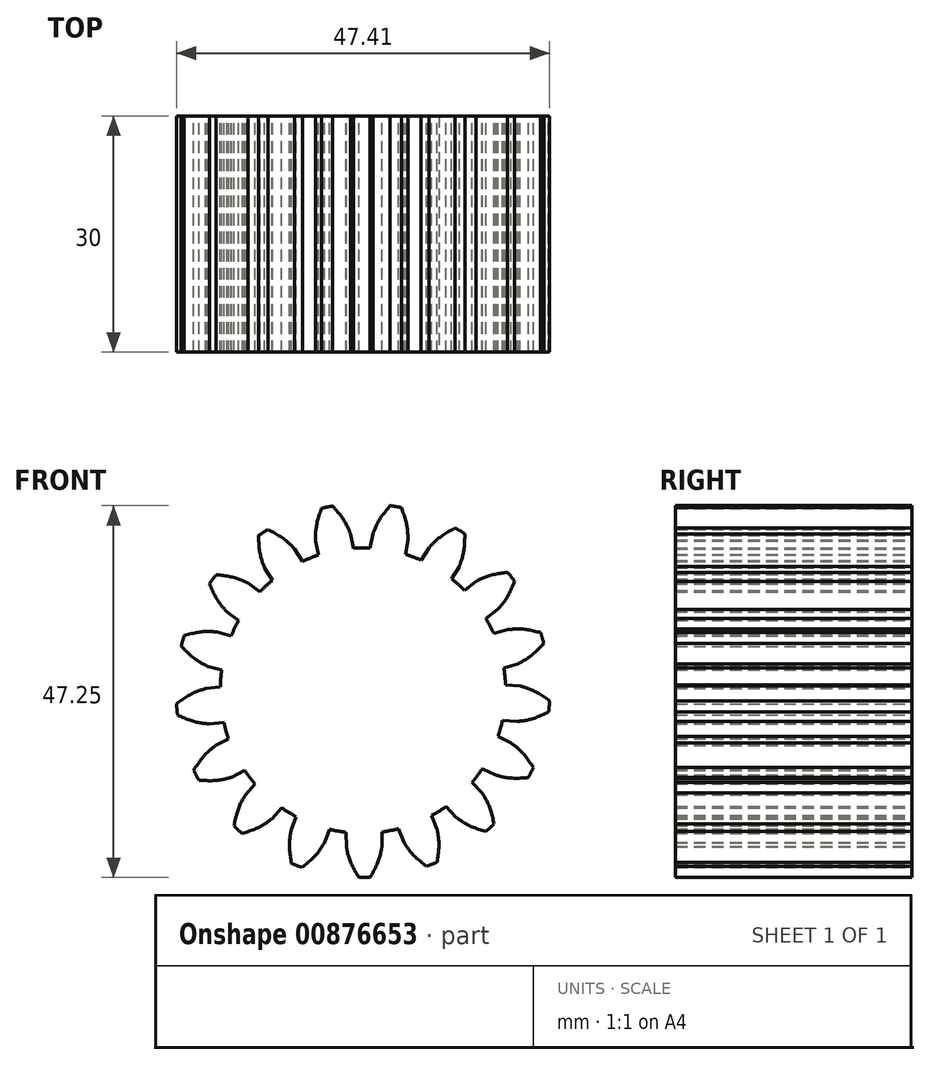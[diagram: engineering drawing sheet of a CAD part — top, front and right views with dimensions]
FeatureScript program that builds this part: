
annotation { "Feature Type Name" : "Feature", "Feature Type Description" : "" }
export const myFeature = defineFeature(function(context is Context, id is Id, definition is map)
    precondition{}
    {
        {
            var Q0;
            Q0=qCreatedBy(makeId("Front.planeOp"),FACE);
            var sketch = newSketch(context, id + "F0", { "sketchPlane" : qUnion([Q0])});
            skCircle(sketch, "E0", {"center": v(0, 0) * mm, "radius": 21.25 * mm, "construction": true});
            skCircle(sketch, "E1.0", {"center": v(0, 0) * mm, "radius": 23.75 * mm});
            skCircle(sketch, "E2.0", {"center": v(0, 0) * mm, "radius": 18.13 * mm});
            skCircle(sketch, "E3", {"center": v(0, 0) * mm, "radius": 19.97 * mm, "construction": true});
            skLineSegment(sketch, "E4", {"start": v(-6.97, 21.25) * mm, "end": v(7.76, 21.25) * mm, "construction": true});
            skPoint(sketch, "E5", {"position": v(0, 21.25) * mm});
            skLineSegment(sketch, "E6", {"start": v(6.83, 18.76) * mm, "end": v(-5.25, 23.16) * mm, "construction": true});
            skLineSegment(sketch, "E7", {"start": v(-5.25, 23.16) * mm, "end": v(0, 0) * mm, "construction": true});
            skLineSegment(sketch, "E8", {"start": v(6.83, 18.76) * mm, "end": v(0, 0) * mm, "construction": true});
            skPoint(sketch, "E9", {"position": v(-6.03, 19.04) * mm});
            skLineSegment(sketch, "E10", {"start": v(0, 0) * mm, "end": v(3.68, 19.63) * mm, "construction": true});
            skLineSegment(sketch, "E11", {"start": v(0, 0) * mm, "end": v(0.43, 19.96) * mm, "construction": true});
            skLineSegment(sketch, "E12", {"start": v(0, 0) * mm, "end": v(-2.84, 19.77) * mm, "construction": true});
            skLineSegment(sketch, "E13", {"start": v(0, 0) * mm, "end": v(-6.03, 19.04) * mm, "construction": true});
            skLineSegment(sketch, "E14", {"start": v(3.68, 19.63) * mm, "end": v(-5.8, 21.4) * mm, "construction": true});
            skLineSegment(sketch, "E15", {"start": v(0.43, 19.96) * mm, "end": v(-6, 20.1) * mm, "construction": true});
            skLineSegment(sketch, "E16", {"start": v(-2.84, 19.77) * mm, "end": v(-6.02, 19.3) * mm, "construction": true});
            skFitSpline(sketch, "E17", {"points": [v(-6.03, 19.04) * mm, v(-6.02, 19.3) * mm, v(-6, 20.1) * mm, v(-5.8, 21.4) * mm, v(-5.25, 23.16) * mm], "startDerivative": vector(0.05, 1.79) * mm, "endDerivative": vector(1.8, 5.21) * mm});
            skPoint(sketch, "E18", {"position": v(-5.98, 20.4) * mm});
            skLineSegment(sketch, "E19", {"start": v(-5.98, 20.4) * mm, "end": v(0, 0) * mm, "construction": true});
            skLineSegment(sketch, "E20", {"start": v(0, 0) * mm, "end": v(-5.17, 26.49) * mm, "construction": true});
            skLineSegment(sketch, "E21", {"start": v(-6.03, 19.04) * mm, "end": v(-5.67, 17.22) * mm});
            skFitSpline(sketch, "E22.MirrorCS", {"points": [v(-1.58, 19.9) * mm, v(-1.69, 20.16) * mm, v(-2, 20.88) * mm, v(-2.68, 22.01) * mm, v(-3.85, 23.44) * mm], "startDerivative": vector(-0.72, 1.64) * mm, "endDerivative": vector(-3.62, 4.16) * mm});
            skLineSegment(sketch, "E23.MirrorCS", {"start": v(-1.58, 19.9) * mm, "end": v(-1.22, 18.08) * mm});
            skSolve(sketch);
        }
        {
            var Q0;
            {var subQ0=sQuery(id+"F0.wireOp",EDGE,"E17");Q0=makeQuery(id+"F0.imprint","IMPRINT",FACE,{"disambiguationData":[TD([[makeQuery(id+"F0.imprint","IMPRINT",EDGE,{"derivedFrom":subQ0}),-1.0]])]});}
            extrude(context, id + "F1", {"entities" : qUnion([Q0]), "depth" : 30 * mm, "offsetDistance" : 25 * mm});
        }
        {
            var Q0;
            Q0=qCreatedBy(makeId("Right.planeOp"),FACE);
            var sketch = newSketch(context, id + "F2", { "sketchPlane" : qUnion([Q0])});
            skLineSegment(sketch, "E24", {"start": v(0, 0) * mm, "end": v(-47.28, 0) * mm, "construction": true});
            skSolve(sketch);
        }
        {
            var Q0;
            Q0=makeQuery(id+"F1.opExtrude","SWEPT_BODY",BODY,{"disambiguationData":[OSD([sQuery(id+"F0.wireOp",EDGE,"E1.0"),sQuery(id+"F0.wireOp",EDGE,"E2.0"),sQuery(id+"F0.wireOp",EDGE,"E17"),sQuery(id+"F0.wireOp",EDGE,"E21"),sQuery(id+"F0.wireOp",EDGE,"E22.MirrorCS"),sQuery(id+"F0.wireOp",EDGE,"E23.MirrorCS")])]});
            var Q1;
            Q1=sQuery(id+"F2.wireOp",EDGE,"E24");
            circularPattern(context, id + "F3", {"entities" : qUnion([Q0]), "axis" : qUnion([Q1]), "angle" : 360 * degree, "instanceCount" : 17, "equalSpace" : true});
        }
        {
            var Q0;
            {var subQ0=sQuery(id+"F0.wireOp",EDGE,"E2.0");var subQ1=makeQuery(id+"F0.imprint","INTERSECT",VERTEX,{"derivedFrom":[subQ0,sQuery(id+"F0.wireOp",EDGE,"E21")]});Q0=makeQuery(id+"F0.imprint","IMPRINT",FACE,{"disambiguationData":[TD([[makeQuery(id+"F0.imprint","IMPRINT",EDGE,{"disambiguationData":[TD([[subQ1,1.0]])],"derivedFrom":subQ0}),1.0]])]});}
            extrude(context, id + "F4", {"entities" : qUnion([Q0]), "operationType" : NewBodyOperationType.ADD, "depth" : 30 * mm, "offsetDistance" : 25 * mm});
        }
    });
